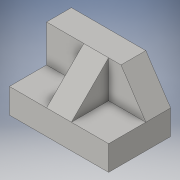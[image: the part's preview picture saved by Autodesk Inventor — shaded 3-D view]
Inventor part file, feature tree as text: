
AUTODESK INVENTOR PART (.ipt)
format: ipt  version: 2016 (Build 200138000, 138)  size: 120,832 bytes
history: native  units: in
note: dims shown in document units (in); Inventor stores cm internally (conversion verified against a paired STEP export)
features: extrude x4, sketch x4
ambient origin geometry x8: Origin, YZ Plane, XZ Plane, XY Plane, X Axis, Y Axis, Z Axis, Center Point
bodies: Solid1 (feature_tree)
feature tree (8):
  extrude  "Extrusion1"  Depth=1.25in
  extrude  "Extrusion2"  Depth=0.5in
  extrude  "Extrusion3"  Depth=0.75in
  extrude  "Extrusion4"  Depth=0.75in TaperAngle=0.0deg
  sketch  "Sketch1"  dims[d0=2.0in d1=1.25in]
  sketch  "Sketch2"  dims[d2=1.25in d3=0.0in d4=0.5in]
  sketch  "Sketch3"  dims[d5=0.5in d6=0.75in]
  sketch  "Sketch4"  dims[d7=0.75in d8=0.75in d9=0.0in d10=0.75in d11=0.0in d12=0.25in d13=0.75in d14=0.0in]
